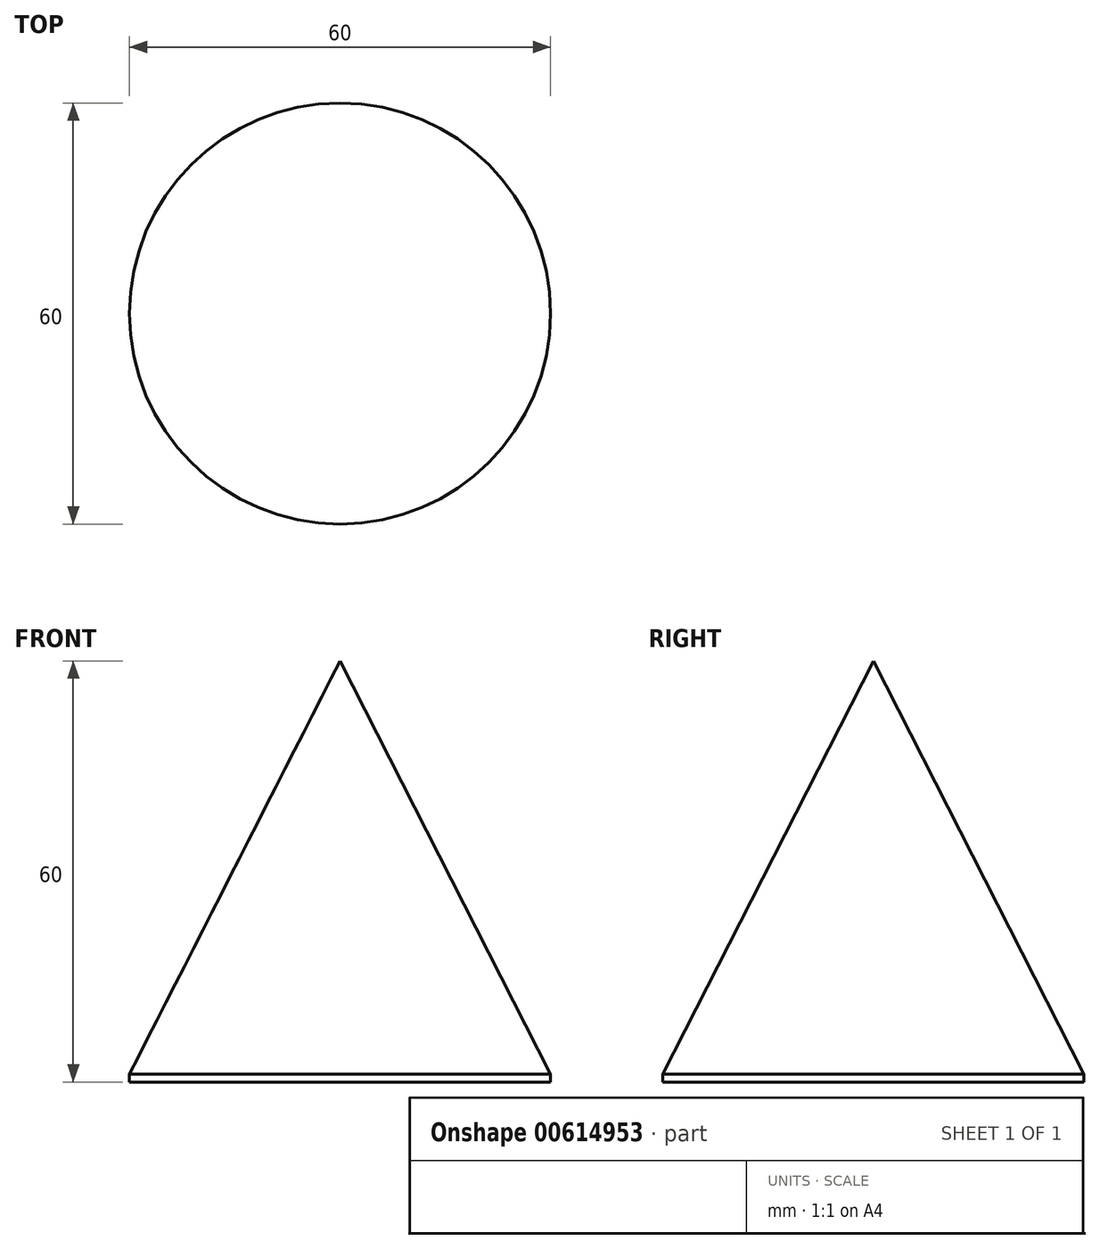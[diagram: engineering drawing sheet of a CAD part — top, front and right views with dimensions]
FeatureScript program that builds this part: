
annotation { "Feature Type Name" : "Feature", "Feature Type Description" : "" }
export const myFeature = defineFeature(function(context is Context, id is Id, definition is map)
    precondition{}
    {
        {
            var Q0;
            Q0=qCreatedBy(makeId("Top.planeOp"),FACE);
            var sketch = newSketch(context, id + "F0", { "sketchPlane" : qUnion([Q0])});
            skCircle(sketch, "E0", {"center": v(0, 0) * mm, "radius": 30 * mm});
            skSolve(sketch);
        }
        {
            var Q0;
            Q0 = qSketchRegion(id + "F0", true);
            extrude(context, id + "F1", {"entities" : qUnion([Q0]), "depth" : 60 * mm, "offsetDistance" : 25 * mm});
        }
        {
            var Q0;
            Q0=makeQuery(id+"F1.opExtrude","CAP_EDGE",EDGE,{"disambiguationData":[OSD([sQuery(id+"F0.wireOp",EDGE,"E0")])],"isStart":false});
            chamfer(context, id + "F2", {"entities" : qUnion([Q0]), "chamferType" : ChamferType.OFFSET_ANGLE, "width" : 30 * mm, "oppositeDirection" : false, "angle" : 63 * degree, "tangentPropagation" : true});
        }
    });
